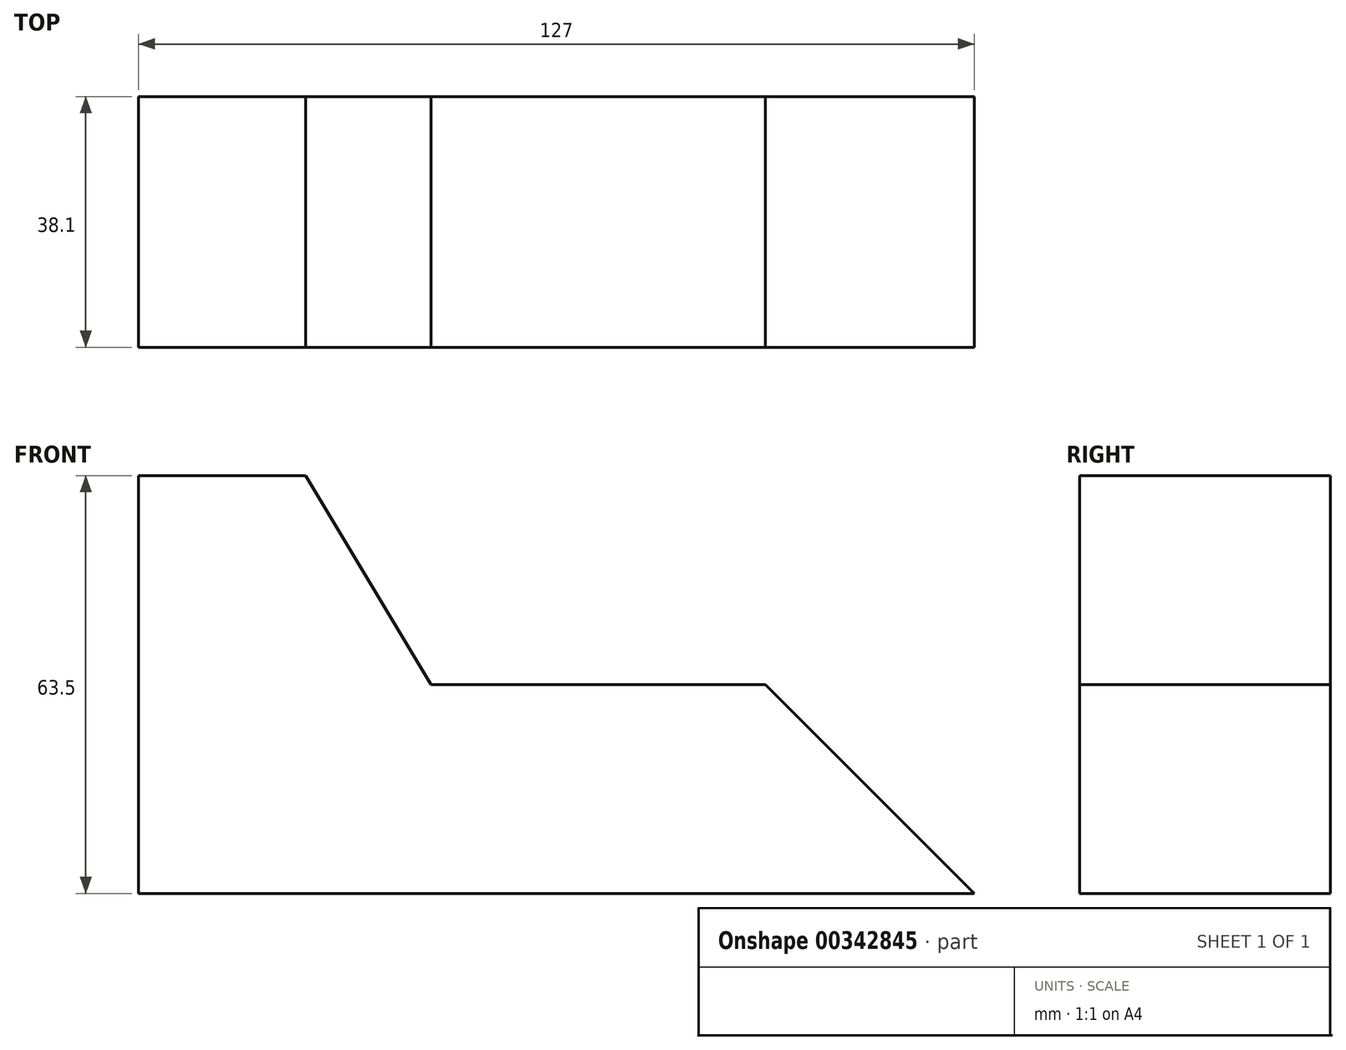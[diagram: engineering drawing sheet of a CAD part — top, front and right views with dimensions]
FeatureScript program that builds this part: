
annotation { "Feature Type Name" : "Feature", "Feature Type Description" : "" }
export const myFeature = defineFeature(function(context is Context, id is Id, definition is map)
    precondition{}
    {
        {
            var Q0;
            Q0=qCreatedBy(makeId("Front.planeOp"),FACE);
            var sketch = newSketch(context, id + "F0", { "sketchPlane" : qUnion([Q0])});
            skLineSegment(sketch, "E0.bottom", {"start": v(-63.5, -31.75) * mm, "end": v(63.5, -31.75) * mm});
            skLineSegment(sketch, "E0.top", {"start": v(-63.5, 31.75) * mm, "end": v(-38.1, 31.75) * mm});
            skLineSegment(sketch, "E0.left", {"start": v(-63.5, -31.75) * mm, "end": v(-63.5, 31.75) * mm});
            skPoint(sketch, "E0.middle", {"position": v(0, 0) * mm});
            skLineSegment(sketch, "E1", {"start": v(63.5, -31.75) * mm, "end": v(31.75, 0) * mm});
            skLineSegment(sketch, "E2", {"start": v(31.75, 0) * mm, "end": v(-19.05, 0) * mm});
            skLineSegment(sketch, "E3", {"start": v(-19.05, 0) * mm, "end": v(-38.1, 31.75) * mm});
            skPoint(sketch, "E4.end.orphan", {"position": v(-19.05, 31.75) * mm});
            skPoint(sketch, "E5.end.orphan", {"position": v(31.75, 31.75) * mm});
            skPoint(sketch, "E6.orphan", {"position": v(63.5, 31.75) * mm});
            skPoint(sketch, "E0.right.end.orphan", {"position": v(63.5, 0) * mm});
            skSolve(sketch);
        }
        {
            var Q0;
            Q0 = qSketchRegion(id + "F0", true);
            extrude(context, id + "F1", {"entities" : qUnion([Q0]), "depth" : 38.1 * mm});
        }
    });
